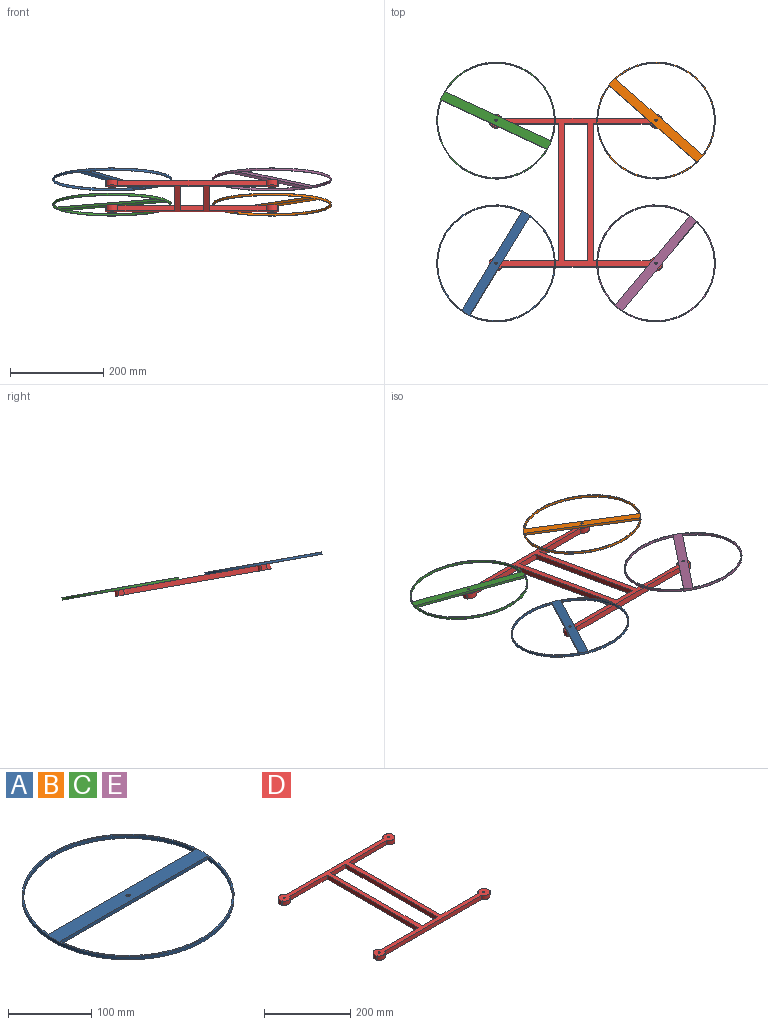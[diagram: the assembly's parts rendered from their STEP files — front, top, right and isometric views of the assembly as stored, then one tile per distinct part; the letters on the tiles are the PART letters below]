
ASSEMBLY  parts=5 mates=8
PART A: 8 faces, bbox 254.8x254.8x5 mm
  f0: plane 249.99x5mm, normal (0,-1,0), area 1249.9mm2, adj f3,f4,f5
  f1: plane 249.99x5mm, normal (0,1,0), area 1249.9mm2, adj f3,f4,f7
  f2: cylinder r=2.5mm len=5mm, axis (0,0,1), area 78.5mm2, adj f3,f4
  f3: plane 254.79x254.79mm, normal (0,0,1), area 6579.1mm2, adj f0,f1,f2,f5,f6,f7
  f4: plane 254.79x254.79mm, normal (0,0,-1), area 6579.1mm2, adj f0,f1,f2,f5,f6,f7
  f5: cylinder r=125.39mm len=249.99mm, axis (0,0,-1), area 1869.6mm2, adj f0,f3,f4
  f6: cylinder r=127.39mm len=254.79mm, axis (0,0,-1), area 4002.2mm2, adj f3,f4
  f7: cylinder r=125.39mm len=249.99mm, axis (0,0,-1), area 1869.6mm2, adj f1,f3,f4
PART B: same geometry as A
PART C: same geometry as A
PART D: 38 faces, bbox 372x340x12 mm
  f0: plane 300x12mm, normal (1,0,0), area 3600mm2, adj f1,f33,f36,f37
  f1: plane 50x12mm, normal (0,-1,0), area 600mm2, adj f0,f2,f36,f37
  f2: plane 300x12mm, normal (-1,0,0), area 3600mm2, adj f1,f33,f36,f37
  f3: plane 12x12mm, normal (1,0,0), area 144mm2, adj f4,f34,f36,f37
  f4: plane 12x1.35mm, normal (0,1,0), area 16.2mm2, adj f3,f5,f36,f37
  f5: cylinder r=14mm len=25.3mm, axis (0,0,-1), area 379mm2, adj f4,f6,f36,f37
  f6: plane 318.7x12mm, normal (0,1,0), area 3824.4mm2, adj f5,f7,f36,f37
  f7: cylinder r=14mm len=25.3mm, axis (0,0,-1), area 379mm2, adj f6,f8,f36,f37
  f8: plane 12x1.35mm, normal (0,1,0), area 16.2mm2, adj f7,f9,f36,f37
  f9: plane 12x12mm, normal (-1,0,0), area 144mm2, adj f8,f10,f36,f37
  f10: plane 12x1.35mm, normal (0,-1,0), area 16.2mm2, adj f9,f11,f36,f37
  f11: cylinder r=14mm len=25.3mm, axis (0,0,-1), area 379mm2, adj f10,f12,f36,f37
  f12: plane 122.35x12mm, normal (0,-1,0), area 1468.2mm2, adj f11,f13,f36,f37
  f13: plane 300x12mm, normal (-1,0,0), area 3600mm2, adj f12,f14,f36,f37
  f14: plane 122.35x12mm, normal (0,1,0), area 1468.2mm2, adj f13,f15,f36,f37
  f15: cylinder r=14mm len=25.3mm, axis (0,0,-1), area 379mm2, adj f14,f16,f36,f37
  f16: plane 12x1.35mm, normal (0,1,0), area 16.2mm2, adj f15,f17,f36,f37
  f17: plane 12x12mm, normal (-1,0,0), area 144mm2, adj f16,f18,f36,f37
  f18: plane 12x1.35mm, normal (0,-1,0), area 16.2mm2, adj f17,f19,f36,f37
  f19: cylinder r=14mm len=25.3mm, axis (0,0,-1), area 379mm2, adj f18,f20,f36,f37
  f20: plane 318.7x12mm, normal (0,-1,0), area 3824.4mm2, adj f19,f21,f36,f37
  f21: cylinder r=14mm len=25.3mm, axis (0,0,-1), area 379mm2, adj f20,f22,f36,f37
  f22: plane 12x1.35mm, normal (0,-1,0), area 16.2mm2, adj f21,f23,f36,f37
  f23: plane 12x12mm, normal (1,0,0), area 144mm2, adj f22,f24,f36,f37
  f24: plane 12x1.35mm, normal (0,1,0), area 16.2mm2, adj f23,f25,f36,f37
  f25: cylinder r=14mm len=25.3mm, axis (0,0,-1), area 379mm2, adj f24,f26,f36,f37
  f26: plane 122.35x12mm, normal (0,1,0), area 1468.2mm2, adj f25,f27,f36,f37
  f27: plane 300x12mm, normal (1,0,0), area 3600mm2, adj f26,f28,f36,f37
  f28: plane 122.35x12mm, normal (0,-1,0), area 1468.2mm2, adj f27,f29,f36,f37
  f29: cylinder r=14mm len=25.3mm, axis (0,0,-1), area 379mm2, adj f28,f34,f36,f37
  f30: cylinder r=2.5mm len=12mm, axis (0,0,-1), area 188.5mm2, adj f36,f37
  f31: cylinder r=2.5mm len=12mm, axis (0,0,-1), area 188.5mm2, adj f36,f37
  f32: cylinder r=2.5mm len=12mm, axis (0,0,-1), area 188.5mm2, adj f36,f37
  f33: plane 50x12mm, normal (0,1,0), area 600mm2, adj f0,f2,f36,f37
  f34: plane 12x1.35mm, normal (0,-1,0), area 16.2mm2, adj f3,f29,f36,f37
  f35: cylinder r=2.5mm len=12mm, axis (0,0,-1), area 188.5mm2, adj f36,f37
  f36: plane 372x340mm, normal (0,0,1), area 17210.8mm2, adj f0,f1,f2,f3,f4,f5,f6,f7
  f37: plane 372x340mm, normal (0,0,-1), area 17210.8mm2, adj f0,f1,f2,f3,f4,f5,f6,f7
PART E: same geometry as A
PLACE A rot(axis=(0.87,0.49,-0.04),171.3deg) t=(-165.92,-194.54,21.39)mm
PLACE B rot(axis=(-0.03,0.09,1),138.6deg) t=(178.08,111.85,-37.71)mm
PLACE C rot(axis=(0.98,-0.22,0.02),170.2deg) t=(-165.92,112.72,-32.79)mm
PLACE D rot(axis=(-1,0,0),10deg) t=(6.08,-42.82,-16.53)mm fixed
PLACE E rot(axis=(-0.18,0.09,0.98),51.6deg) t=(178.08,-195.41,16.47)mm
MATE cylindrical A.f2 <-> D.f15  axis (0,0.17,0.98) through (-165.92,-194.54,21.39)mm
MATE planar D.f36 <-> E.f2  axis (0,0.17,0.98) through (6.08,-41.78,-10.62)mm
MATE cylindrical C.f2 <-> D.f7  axis (0,0.17,0.98) through (-165.92,112.72,-32.79)mm
MATE cylindrical B.f2 <-> D.f5  axis (0,0.17,0.98) through (178.08,112.72,-32.79)mm
MATE planar D.f36 <-> C.f2  axis (0,0.17,0.98) through (6.08,-41.78,-10.62)mm
MATE cylindrical E.f2 <-> D.f21  axis (0,0.17,0.98) through (178.08,-194.54,21.39)mm
MATE planar B.f2 <-> D.f36  axis (0,-0.17,-0.98) through (178.08,111.85,-37.71)mm
MATE planar D.f36 <-> A.f2  axis (0,0.17,0.98) through (6.08,-41.78,-10.62)mm
